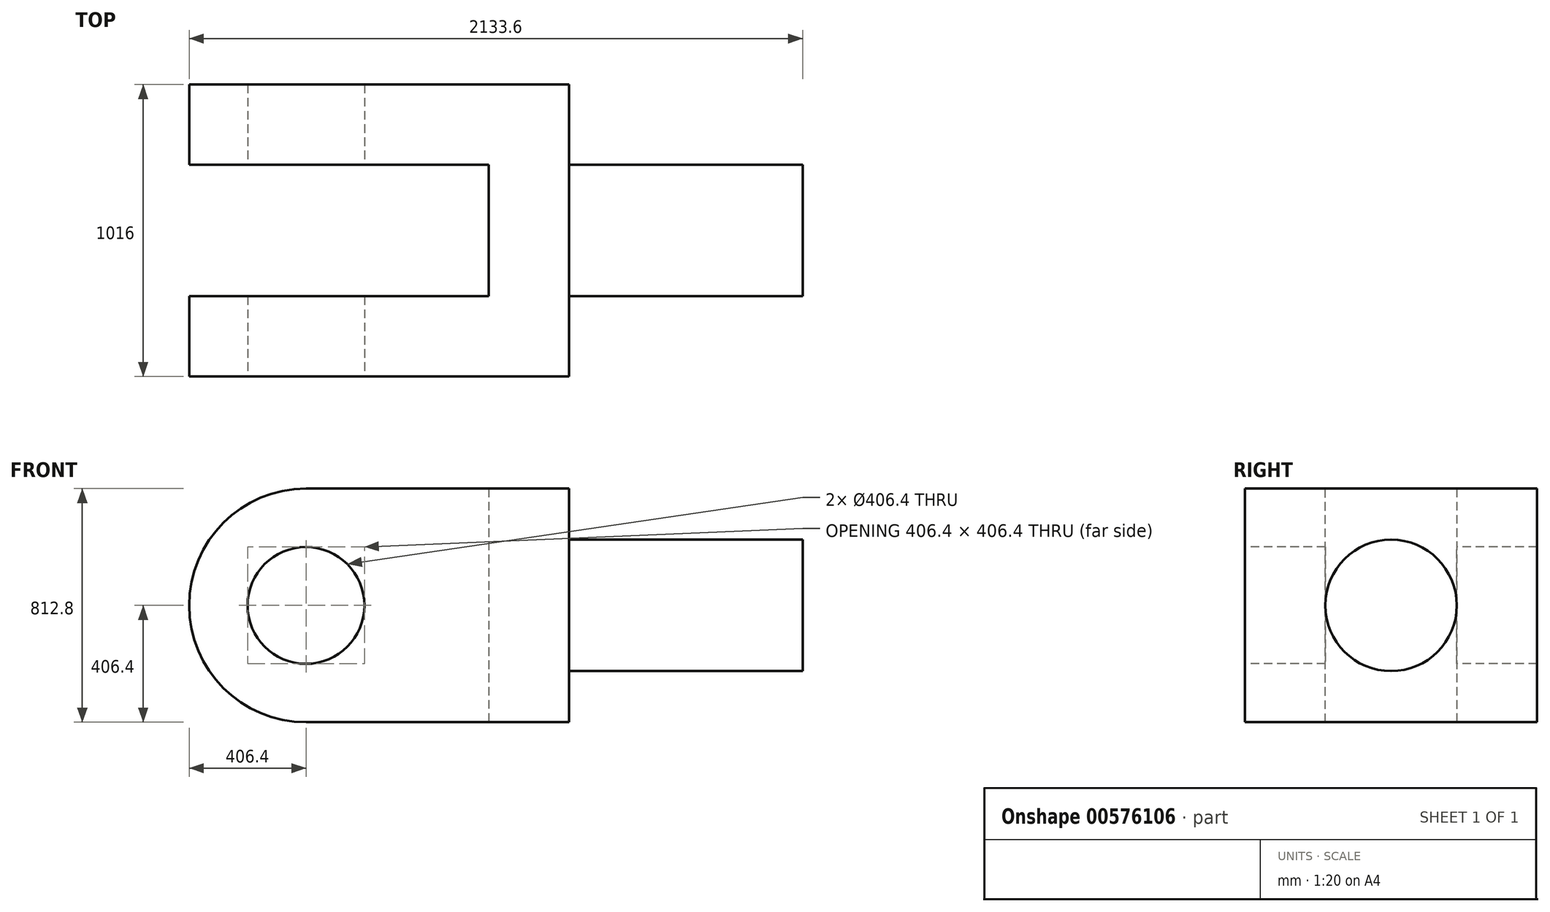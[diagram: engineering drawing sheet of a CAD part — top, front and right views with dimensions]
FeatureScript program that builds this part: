
annotation { "Feature Type Name" : "Feature", "Feature Type Description" : "" }
export const myFeature = defineFeature(function(context is Context, id is Id, definition is map)
    precondition{}
    {
        {
            var Q0;
            Q0=qCreatedBy(makeId("Top.planeOp"),FACE);
            var sketch = newSketch(context, id + "F0", { "sketchPlane" : qUnion([Q0])});
            skLineSegment(sketch, "E0", {"start": v(0, 0) * mm, "end": v(1320.8, 0) * mm});
            skLineSegment(sketch, "E1", {"start": v(1320.8, 0) * mm, "end": v(1320.8, -279.4) * mm});
            skLineSegment(sketch, "E2", {"start": v(1320.8, -279.4) * mm, "end": v(1320.8, -736.6) * mm});
            skLineSegment(sketch, "E3", {"start": v(1320.8, -736.6) * mm, "end": v(1320.8, -1016) * mm});
            skPoint(sketch, "E3.endSnap0", {"position": v(1320.8, -508) * mm});
            skLineSegment(sketch, "E4", {"start": v(1320.8, -1016) * mm, "end": v(0, -1016) * mm});
            skLineSegment(sketch, "E5", {"start": v(0, -1016) * mm, "end": v(0, -736.6) * mm});
            skLineSegment(sketch, "E6", {"start": v(0, -736.6) * mm, "end": v(1041.4, -736.6) * mm});
            skLineSegment(sketch, "E7", {"start": v(1041.4, -736.6) * mm, "end": v(1041.4, -279.4) * mm});
            skLineSegment(sketch, "E8", {"start": v(1041.4, -279.4) * mm, "end": v(0, -279.4) * mm});
            skLineSegment(sketch, "E9", {"start": v(0, -279.4) * mm, "end": v(0, 0) * mm});
            skLineSegment(sketch, "E10", {"start": v(1320.8, -279.4) * mm, "end": v(2133.6, -279.4) * mm});
            skLineSegment(sketch, "E11", {"start": v(1320.8, -736.6) * mm, "end": v(2133.6, -736.6) * mm});
            skLineSegment(sketch, "E12", {"start": v(2133.6, -736.6) * mm, "end": v(2133.6, -279.4) * mm});
            skSolve(sketch);
        }
        {
            var Q0;
            Q0=makeQuery(id+"F0.imprint","IMPRINT",FACE,{"disambiguationData":[TD([[makeQuery(id+"F0.imprint","IMPRINT",EDGE,{"derivedFrom":sQuery(id+"F0.wireOp",EDGE,"E0")}),-1.0]])]});
            extrude(context, id + "F1", {"entities" : qUnion([Q0]), "depth" : 406.4 * mm, "offsetDistance" : 25.4 * mm});
        }
        {
            var Q0;
            Q0=makeQuery(id+"F0.imprint","IMPRINT",FACE,{"disambiguationData":[TD([[makeQuery(id+"F0.imprint","IMPRINT",EDGE,{"derivedFrom":sQuery(id+"F0.wireOp",EDGE,"E0")}),-1.0]])]});
            extrude(context, id + "F2", {"entities" : qUnion([Q0]), "operationType" : NewBodyOperationType.ADD, "oppositeDirection" : true, "depth" : 406.4 * mm, "offsetDistance" : 25.4 * mm});
        }
        {
            var Q0;
            Q0=makeQuery(id+"F0.imprint","IMPRINT",FACE,{"disambiguationData":[TD([[makeQuery(id+"F0.imprint","IMPRINT",EDGE,{"derivedFrom":sQuery(id+"F0.wireOp",EDGE,"E2")}),1.0]])]});
            extrude(context, id + "F3", {"entities" : qUnion([Q0]), "operationType" : NewBodyOperationType.ADD, "depth" : 228.6 * mm, "offsetDistance" : 25.4 * mm});
        }
        {
            var Q0;
            Q0=makeQuery(id+"F0.imprint","IMPRINT",FACE,{"disambiguationData":[TD([[makeQuery(id+"F0.imprint","IMPRINT",EDGE,{"derivedFrom":sQuery(id+"F0.wireOp",EDGE,"E2")}),1.0]])]});
            extrude(context, id + "F4", {"entities" : qUnion([Q0]), "operationType" : NewBodyOperationType.ADD, "oppositeDirection" : true, "depth" : 228.6 * mm, "offsetDistance" : 25.4 * mm});
        }
        {
            var Q0;
            {var subQ0=sQuery(id+"F0.wireOp",EDGE,"E4");Q0=makeQuery(id+"F2.boolean.opBoolean","MERGE",FACE,{"derivedFrom":[makeQuery(id+"F1.opExtrude","SWEPT_FACE",FACE,{"disambiguationData":[OSD([subQ0])]}),makeQuery(id+"F2.opExtrude","SWEPT_FACE",FACE,{"disambiguationData":[OSD([subQ0])]})]});}
            var sketch = newSketch(context, id + "F5", { "sketchPlane" : qUnion([Q0])});
            skPoint(sketch, "E13.endSnap0", {"position": v(1320.8, 0) * mm});
            skCircle(sketch, "E14", {"center": v(406.4, 0) * mm, "radius": 203.2 * mm});
            skSolve(sketch);
        }
        {
            var Q0;
            Q0=makeQuery(id+"F5.imprint","IMPRINT",FACE,{"disambiguationData":[TD([[makeQuery(id+"F5.imprint","IMPRINT",EDGE,{"derivedFrom":sQuery(id+"F5.wireOp",EDGE,"E14")}),1.0]])]});
            extrude(context, id + "F6", {"entities" : qUnion([Q0]), "operationType" : NewBodyOperationType.REMOVE, "oppositeDirection" : true, "depth" : 1270 * mm, "offsetDistance" : 25.4 * mm});
        }
        {
            var Q0;
            {var subQ0=sQuery(id+"F0.wireOp",EDGE,"E4");Q0=makeQuery(id+"F2.boolean.opBoolean","MERGE",FACE,{"derivedFrom":[makeQuery(id+"F1.opExtrude","SWEPT_FACE",FACE,{"disambiguationData":[OSD([subQ0])]}),makeQuery(id+"F2.opExtrude","SWEPT_FACE",FACE,{"disambiguationData":[OSD([subQ0])]})]});}
            var sketch = newSketch(context, id + "F7", { "sketchPlane" : qUnion([Q0])});
            skCircle(sketch, "E15", {"center": v(406.4, 0) * mm, "radius": 406.4 * mm});
            skSolve(sketch);
        }
        {
            var Q0;
            {var subQ0=sQuery(id+"F7.wireOp",EDGE,"E15");var subQ2=sQuery(id+"F0.wireOp",EDGE,"E4");var subQ5=makeQuery(id+"F1.opExtrude","CAP_EDGE",EDGE,{"disambiguationData":[OSD([subQ2])],"isStart":false});var subQ6=makeQuery(id+"F7.imprint","INTERSECT",VERTEX,{"derivedFrom":[subQ5,subQ0]});Q0=makeQuery(id+"F7.imprint","IMPRINT",FACE,{"disambiguationData":[TD([[makeQuery(id+"F7.imprint","IMPRINT",EDGE,{"disambiguationData":[TD([[subQ6,-1.0]])],"derivedFrom":subQ0}),-1.0]])]});}
            var Q1;
            {var subQ0=sQuery(id+"F7.wireOp",EDGE,"E15");var subQ2=sQuery(id+"F0.wireOp",EDGE,"E4");var subQ5=makeQuery(id+"F2.opExtrude","CAP_EDGE",EDGE,{"disambiguationData":[OSD([subQ2])],"isStart":false});var subQ6=makeQuery(id+"F7.imprint","INTERSECT",VERTEX,{"derivedFrom":[subQ5,subQ0]});Q1=makeQuery(id+"F7.imprint","IMPRINT",FACE,{"disambiguationData":[TD([[makeQuery(id+"F7.imprint","IMPRINT",EDGE,{"disambiguationData":[TD([[subQ6,1.0]])],"derivedFrom":subQ0}),-1.0]])]});}
            extrude(context, id + "F8", {"entities" : qUnion([Q0, Q1]), "operationType" : NewBodyOperationType.REMOVE, "oppositeDirection" : true, "depth" : 1270 * mm, "offsetDistance" : 25.4 * mm});
        }
        {
            var Q0;
            {var subQ0=sQuery(id+"F0.wireOp",EDGE,"E12");Q0=makeQuery(id+"F4.boolean.opBoolean","MERGE",FACE,{"derivedFrom":[makeQuery(id+"F3.opExtrude","SWEPT_FACE",FACE,{"disambiguationData":[OSD([subQ0])]}),makeQuery(id+"F4.opExtrude","SWEPT_FACE",FACE,{"disambiguationData":[OSD([subQ0])]})]});}
            var sketch = newSketch(context, id + "F9", { "sketchPlane" : qUnion([Q0])});
            skPoint(sketch, "E16.endSnap0", {"position": v(-508, 228.6) * mm});
            skCircle(sketch, "E17", {"center": v(-508, 0) * mm, "radius": 228.6 * mm});
            skSolve(sketch);
        }
        {
            var Q0;
            {var subQ0=sQuery(id+"F9.wireOp",EDGE,"E17");var subQ1=sQuery(id+"F0.wireOp",EDGE,"E12");var subQ2=makeQuery(id+"F3.opExtrude","CAP_EDGE",EDGE,{"disambiguationData":[OSD([subQ1])],"isStart":false});var subQ3=makeQuery(id+"F9.imprint","INTERSECT",VERTEX,{"derivedFrom":[subQ2,subQ0]});Q0=makeQuery(id+"F9.imprint","IMPRINT",FACE,{"disambiguationData":[TD([[makeQuery(id+"F9.imprint","IMPRINT",EDGE,{"disambiguationData":[TD([[subQ3,-1.0]])],"derivedFrom":subQ0}),-1.0]])]});}
            var Q1;
            {var subQ0=sQuery(id+"F9.wireOp",EDGE,"E17");var subQ1=sQuery(id+"F0.wireOp",EDGE,"E12");var subQ2=makeQuery(id+"F3.opExtrude","CAP_EDGE",EDGE,{"disambiguationData":[OSD([subQ1])],"isStart":false});var subQ3=makeQuery(id+"F9.imprint","INTERSECT",VERTEX,{"derivedFrom":[subQ2,subQ0]});Q1=makeQuery(id+"F9.imprint","IMPRINT",FACE,{"disambiguationData":[TD([[makeQuery(id+"F9.imprint","IMPRINT",EDGE,{"disambiguationData":[TD([[subQ3,1.0]])],"derivedFrom":subQ0}),-1.0]])]});}
            var Q2;
            {var subQ0=sQuery(id+"F9.wireOp",EDGE,"E17");var subQ1=sQuery(id+"F0.wireOp",EDGE,"E12");var subQ5=makeQuery(id+"F4.opExtrude","CAP_EDGE",EDGE,{"disambiguationData":[OSD([subQ1])],"isStart":false});var subQ6=makeQuery(id+"F9.imprint","INTERSECT",VERTEX,{"derivedFrom":[subQ5,subQ0]});Q2=makeQuery(id+"F9.imprint","IMPRINT",FACE,{"disambiguationData":[TD([[makeQuery(id+"F9.imprint","IMPRINT",EDGE,{"disambiguationData":[TD([[subQ6,-1.0]])],"derivedFrom":subQ0}),-1.0]])]});}
            var Q3;
            {var subQ0=sQuery(id+"F9.wireOp",EDGE,"E17");var subQ1=sQuery(id+"F0.wireOp",EDGE,"E12");var subQ5=makeQuery(id+"F4.opExtrude","CAP_EDGE",EDGE,{"disambiguationData":[OSD([subQ1])],"isStart":false});var subQ6=makeQuery(id+"F9.imprint","INTERSECT",VERTEX,{"derivedFrom":[subQ5,subQ0]});Q3=makeQuery(id+"F9.imprint","IMPRINT",FACE,{"disambiguationData":[TD([[makeQuery(id+"F9.imprint","IMPRINT",EDGE,{"disambiguationData":[TD([[subQ6,1.0]])],"derivedFrom":subQ0}),-1.0]])]});}
            extrude(context, id + "F10", {"entities" : qUnion([Q0, Q1, Q2, Q3]), "operationType" : NewBodyOperationType.REMOVE, "oppositeDirection" : true, "depth" : 812.8 * mm, "offsetDistance" : 25.4 * mm});
        }
    });
